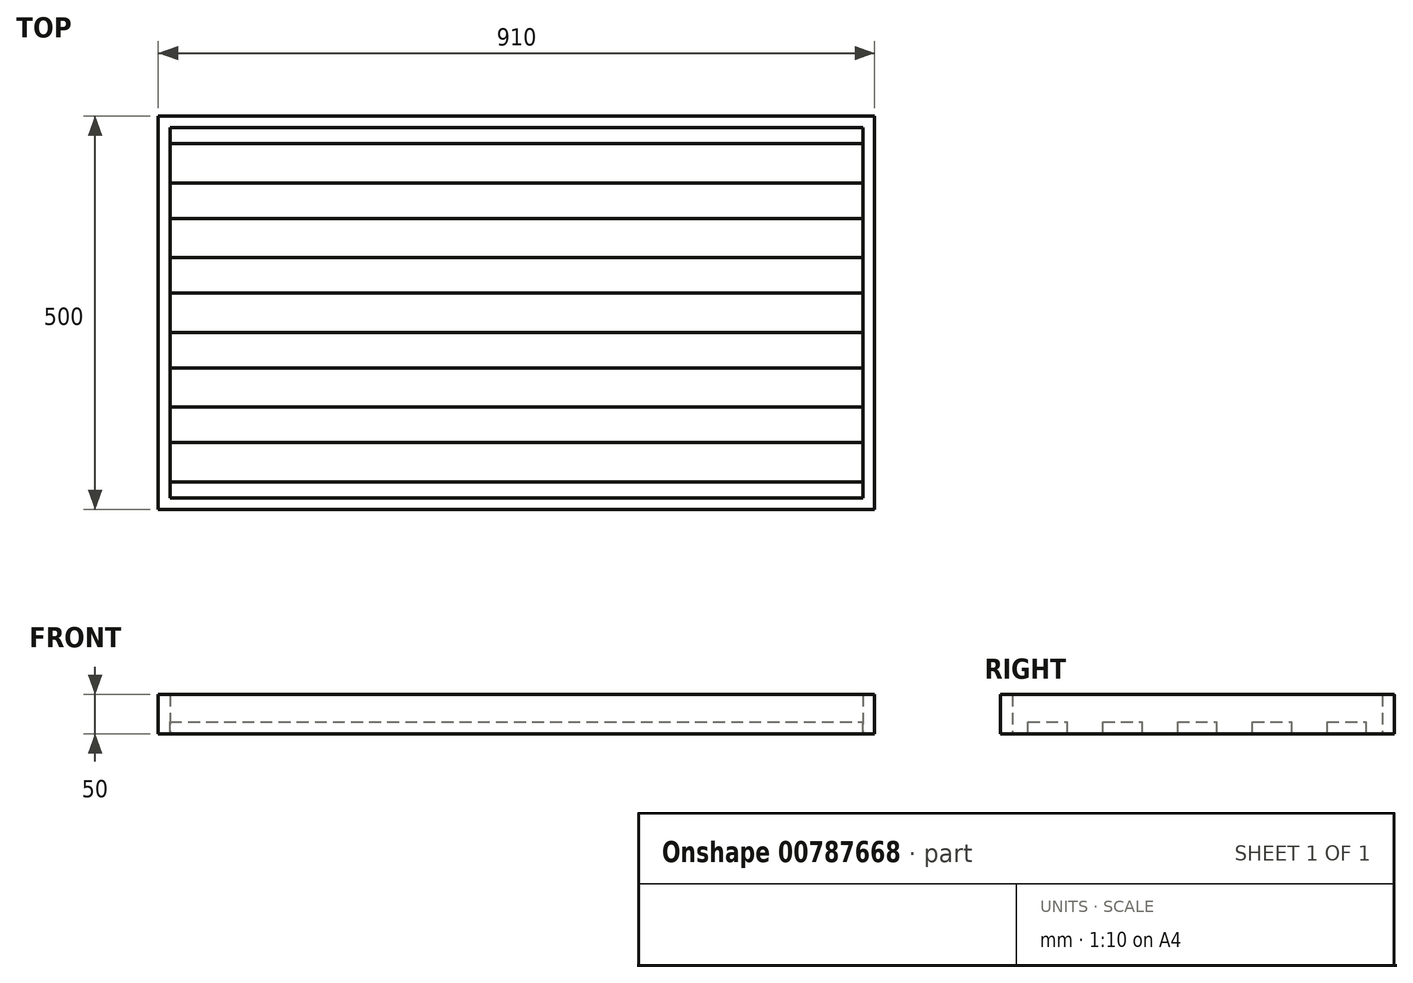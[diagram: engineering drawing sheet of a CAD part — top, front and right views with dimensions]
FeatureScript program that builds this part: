
annotation { "Feature Type Name" : "Feature", "Feature Type Description" : "" }
export const myFeature = defineFeature(function(context is Context, id is Id, definition is map)
    precondition{}
    {
        {
            var Q0;
            Q0=qCreatedBy(makeId("Top.planeOp"),FACE);
            var sketch = newSketch(context, id + "F0", { "sketchPlane" : qUnion([Q0])});
            skLineSegment(sketch, "E0.bottom", {"start": v(-455, -250) * mm, "end": v(455, -250) * mm});
            skLineSegment(sketch, "E0.top", {"start": v(-455, 250) * mm, "end": v(455, 250) * mm});
            skLineSegment(sketch, "E0.left", {"start": v(-455, -250) * mm, "end": v(-455, 250) * mm});
            skLineSegment(sketch, "E0.right", {"start": v(455, -250) * mm, "end": v(455, 250) * mm});
            skPoint(sketch, "E0.middle", {"position": v(0, 0) * mm});
            skLineSegment(sketch, "E1.0", {"start": v(-440, 235) * mm, "end": v(440, 235) * mm});
            skLineSegment(sketch, "E1.1", {"start": v(-440, -235) * mm, "end": v(-440, 235) * mm});
            skLineSegment(sketch, "E1.2", {"start": v(-440, -235) * mm, "end": v(440, -235) * mm});
            skLineSegment(sketch, "E1.3", {"start": v(440, -235) * mm, "end": v(440, 235) * mm});
            skSolve(sketch);
        }
        {
            var Q0;
            Q0 = qSketchRegion(id + "F0", true);
            extrude(context, id + "F1", {"entities" : qUnion([Q0]), "depth" : 50 * mm, "offsetDistance" : 25 * mm});
        }
        {
            var Q0;
            Q0=makeQuery(id+"F0.imprint","IMPRINT",FACE,{"disambiguationData":[TD([[makeQuery(id+"F0.imprint","IMPRINT",EDGE,{"derivedFrom":sQuery(id+"F0.wireOp",EDGE,"E1.0")}),-1.0]])]});
            extrude(context, id + "F2", {"entities" : qUnion([Q0]), "operationType" : NewBodyOperationType.ADD, "depth" : 15 * mm, "offsetDistance" : 25 * mm});
        }
        {
            var Q0;
            Q0=makeQuery(id+"F2.opExtrude","CAP_FACE",FACE,{"disambiguationData":[OSD([sQuery(id+"F0.wireOp",EDGE,"E1.0"),sQuery(id+"F0.wireOp",EDGE,"E1.1"),sQuery(id+"F0.wireOp",EDGE,"E1.2"),sQuery(id+"F0.wireOp",EDGE,"E1.3")])],"isStart":false});
            var sketch = newSketch(context, id + "F3", { "sketchPlane" : qUnion([Q0])});
            skLineSegment(sketch, "E2.bottom", {"start": v(-440, 165) * mm, "end": v(440, 165) * mm});
            skLineSegment(sketch, "E2.top", {"start": v(-440, 120) * mm, "end": v(440, 120) * mm});
            skLineSegment(sketch, "E2.left", {"start": v(-440, 165) * mm, "end": v(-440, 120) * mm});
            skLineSegment(sketch, "E2.right", {"start": v(440, 165) * mm, "end": v(440, 120) * mm});
            skLineSegment(sketch, "E3.bottom", {"start": v(-440, 70) * mm, "end": v(440, 70) * mm});
            skLineSegment(sketch, "E3.top", {"start": v(-440, 25) * mm, "end": v(440, 25) * mm});
            skLineSegment(sketch, "E3.left", {"start": v(-440, 70) * mm, "end": v(-440, 25) * mm});
            skLineSegment(sketch, "E3.right", {"start": v(440, 70) * mm, "end": v(440, 25) * mm});
            skLineSegment(sketch, "E4.bottom", {"start": v(-440, -25) * mm, "end": v(440, -25) * mm});
            skLineSegment(sketch, "E4.top", {"start": v(-440, -70) * mm, "end": v(440, -70) * mm});
            skLineSegment(sketch, "E4.left", {"start": v(-440, -25) * mm, "end": v(-440, -70) * mm});
            skLineSegment(sketch, "E4.right", {"start": v(440, -25) * mm, "end": v(440, -70) * mm});
            skLineSegment(sketch, "E5.bottom", {"start": v(-440, -120) * mm, "end": v(440, -120) * mm});
            skLineSegment(sketch, "E5.top", {"start": v(-440, -165) * mm, "end": v(440, -165) * mm});
            skLineSegment(sketch, "E5.left", {"start": v(-440, -120) * mm, "end": v(-440, -165) * mm});
            skLineSegment(sketch, "E5.right", {"start": v(440, -120) * mm, "end": v(440, -165) * mm});
            skLineSegment(sketch, "E6", {"start": v(0, 25) * mm, "end": v(0, -25) * mm, "construction": true});
            skLineSegment(sketch, "E7", {"start": v(0, 120) * mm, "end": v(0, 70) * mm, "construction": true});
            skLineSegment(sketch, "E8", {"start": v(0, -70) * mm, "end": v(0, -120) * mm, "construction": true});
            skLineSegment(sketch, "E9.bottom", {"start": v(-440, 235) * mm, "end": v(440, 235) * mm});
            skLineSegment(sketch, "E9.top", {"start": v(-440, 215) * mm, "end": v(440, 215) * mm});
            skLineSegment(sketch, "E9.left", {"start": v(-440, 235) * mm, "end": v(-440, 215) * mm});
            skLineSegment(sketch, "E9.right", {"start": v(440, 235) * mm, "end": v(440, 215) * mm});
            skLineSegment(sketch, "E10.bottom", {"start": v(-440, -235) * mm, "end": v(440, -235) * mm});
            skLineSegment(sketch, "E10.top", {"start": v(-440, -215) * mm, "end": v(440, -215) * mm});
            skLineSegment(sketch, "E10.left", {"start": v(-440, -235) * mm, "end": v(-440, -215) * mm});
            skLineSegment(sketch, "E10.right", {"start": v(440, -235) * mm, "end": v(440, -215) * mm});
            skLineSegment(sketch, "E11", {"start": v(0, -165) * mm, "end": v(0, -215) * mm, "construction": true});
            skLineSegment(sketch, "E12", {"start": v(0, 165) * mm, "end": v(0, 215) * mm, "construction": true});
            skSolve(sketch);
        }
        {
            var Q0;
            Q0 = qSketchRegion(id + "F3", true);
            extrude(context, id + "F4", {"entities" : qUnion([Q0]), "operationType" : NewBodyOperationType.REMOVE, "endBound" : BoundingType.UP_TO_NEXT, "oppositeDirection" : true, "depth" : 20 * mm, "offsetDistance" : 25 * mm});
        }
    });
